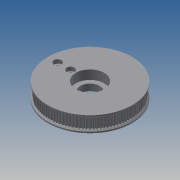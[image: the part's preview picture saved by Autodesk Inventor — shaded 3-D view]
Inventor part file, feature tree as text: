
AUTODESK INVENTOR PART (.ipt)
format: ipt  version: 2013 (Build 170138000, 138)  size: 1,207,808 bytes
history: native  units: mm
features: extrude x5, sketch x5, pattern_circular x1, chamfer x1, mirror x1
ambient origin geometry x8: Origin, YZ Plane, XZ Plane, XY Plane, X Axis, Y Axis, Z Axis, Center Point
bodies: Solid1 (feature_tree)
feature tree (13):
  extrude  "Extrusion1"  Depth=0.628319mm
  pattern_circular  "Circular Pattern1"  [2 undecoded]
  extrude  "Extrusion3"  Depth=0.75mm
  chamfer  "Chamfer2"  Distance=0.254mm
  mirror  "Mirror1"
  extrude  "Extrusion4"  Depth=8.0mm TaperAngle=0.0deg
  extrude  "Extrusion5"  Depth=1000.0mm
  extrude  "Extrusion6"  TaperAngle=360.0deg  [1 undecoded]
  sketch  "Sketch1"  dims[d0=63.661977mm d9=0.628319mm]
  sketch  "Sketch3"  dims[d11=0.254mm]
  sketch  "Sketch4"  dims[d12=0.3mm]
  sketch  "Sketch5"  dims[d13=0.4mm]
  sketch  "Sketch6"  dims[d14=1.0mm d15=0.555mm d16=0.75mm d17=0.254mm d18=8.0mm d19=0.0mm d20=1000.0mm d21=360.0deg d23=0.1mm d32=2.0mm d33=0.0mm d34=1.0mm d35=2.0mm d36=45.0deg d37=15.0mm d39=3.5mm d40=15.0mm d41=25.0mm d42=2.0mm d43=0.0mm d44=6.0mm d46=3.0mm d47=0.0mm d49=22.0mm d51=7.0mm d52=0.0mm d53=1.0mm]
note: 3 required parameter values undecoded (feature->parameter linkage not recoverable at this tier; creation-order binding heuristic only, values carry confidence <= 0.55)
